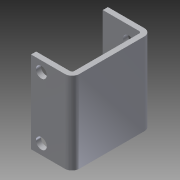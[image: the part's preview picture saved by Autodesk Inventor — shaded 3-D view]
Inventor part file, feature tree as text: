
AUTODESK INVENTOR PART (.ipt)
format: ipt  version: 2013 (Build 170138000, 138)  size: 168,960 bytes
history: native  units: in
note: dims shown in document units (in); Inventor stores cm internally (conversion verified against a paired STEP export)
features: reference x8, sheet_metal_op x7, sketch x7, other x5, extrude x2
ambient origin geometry x8: Origin, YZ Plane, XZ Plane, XY Plane, X Axis, Y Axis, Z Axis, Center Point
bodies: Solid1 (feature_tree)
feature tree (29):
  sheet_metal_op  "Face1"
  sheet_metal_op  "Flange1"
  sheet_metal_op  "Flange2"
  extrude  "Extrusion1"  Depth=2.0in
  extrude  "Extrusion2"  Depth=0.125in
  sketch  "Sketch1"  dims[d0=1.0in d1=2.0in]
  other  "Plate1"
  sketch  "Sketch2"  dims[d2=0.125in d3=0.125in]
  other  "Plate2"
  sheet_metal_op  "Bend1"
  sheet_metal_op  "Corner1"
  sketch  "Sketch3"  dims[d4=0.0625in]
  other  "Plate3"
  sheet_metal_op  "Bend2"
  sheet_metal_op  "Corner2"
  sketch  "Sketch4"  dims[d5=0.25in]
  sketch  "Sketch5"  dims[d6=0.125in]
  sketch  "Sketch6"  dims[d7=1.9375in d8=90.0deg d9=0.05in]
  reference  "Reference1"
  reference  "Reference2"
  sketch  "Sketch8"  dims[d10=0.5in d11=0.125in d12=0.125in d13=0.125in d14=0.0625in d15=0.25in d16=0.125in d17=1.0in d18=90.0deg d19=0.05in d20=0.5in d21=0.125in d22=0.125in d23=0.564in d24=0.0in d25=0.5in d26=0.0in d27=0.75in d28=0.125in d29=0.0in d32=0.125in d33=0.0in]
  reference  "Reference8"
  reference  "Reference9"
  reference  "Reference10"
  reference  "Reference11"
  reference  "Reference12"
  reference  "Reference13"
  other  "Cut1"
  other  "Cut3"
